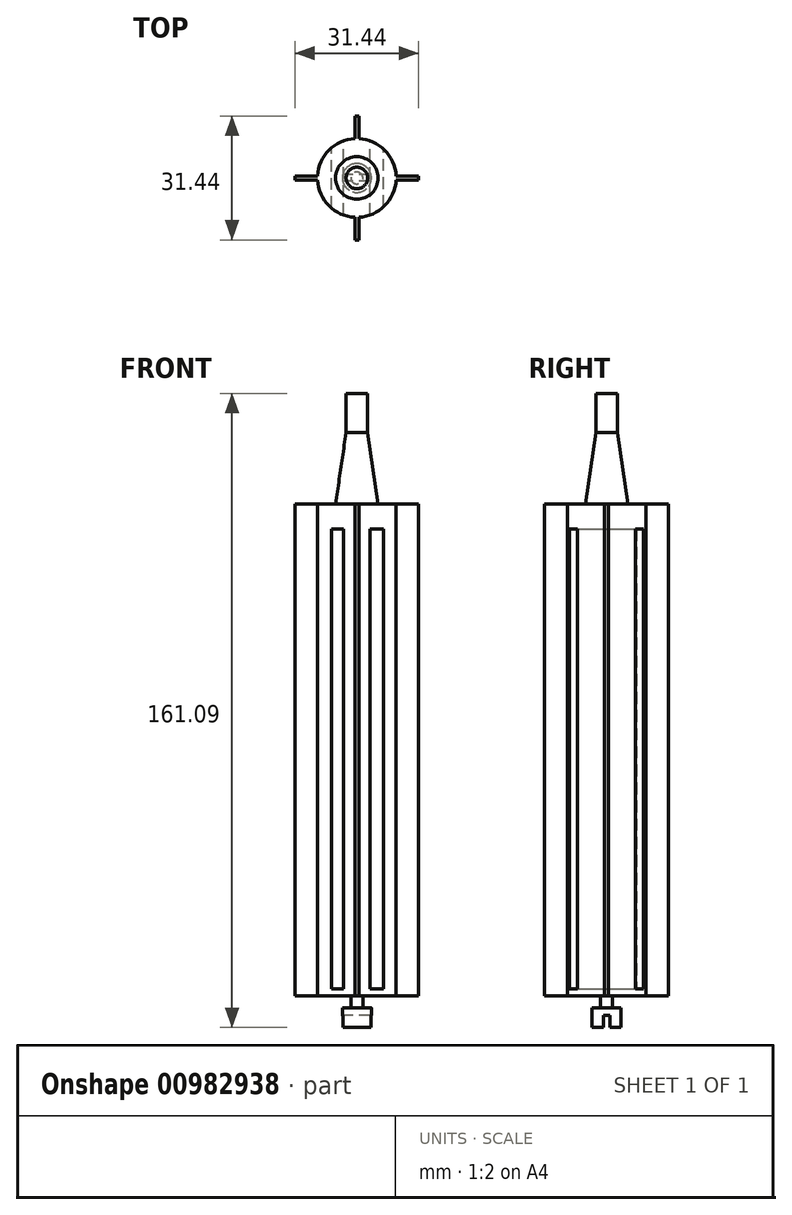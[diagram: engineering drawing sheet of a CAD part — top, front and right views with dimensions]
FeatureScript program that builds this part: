
annotation { "Feature Type Name" : "Feature", "Feature Type Description" : "" }
export const myFeature = defineFeature(function(context is Context, id is Id, definition is map)
    precondition{}
    {
        {
            var Q0;
            Q0=qCreatedBy(makeId("Top.planeOp"),FACE);
            var sketch = newSketch(context, id + "F0", { "sketchPlane" : qUnion([Q0])});
            skCircle(sketch, "E0", {"center": v(0, 0) * mm, "radius": 10 * mm});
            skLineSegment(sketch, "E1.bottom", {"start": v(-0.5, 15.72) * mm, "end": v(0.5, 15.72) * mm});
            skLineSegment(sketch, "E1.top", {"start": v(-0.5, 2) * mm, "end": v(0.5, 2) * mm});
            skLineSegment(sketch, "E1.left", {"start": v(-0.5, 15.72) * mm, "end": v(-0.5, 2) * mm});
            skLineSegment(sketch, "E1.right", {"start": v(0.5, 15.72) * mm, "end": v(0.5, 2) * mm});
            skPoint(sketch, "E2.center", {"position": v(0, -8) * mm});
            skLineSegment(sketch, "E3.1.0", {"start": v(-15.72, -0.5) * mm, "end": v(-2, -0.5) * mm});
            skLineSegment(sketch, "E3.1.1", {"start": v(-15.72, 0.5) * mm, "end": v(-2, 0.5) * mm});
            skLineSegment(sketch, "E3.1.2", {"start": v(-15.72, -0.5) * mm, "end": v(-15.72, 0.5) * mm});
            skLineSegment(sketch, "E3.1.3", {"start": v(-2, -0.5) * mm, "end": v(-2, 0.5) * mm});
            skLineSegment(sketch, "E3.2.0", {"start": v(0.5, -15.72) * mm, "end": v(0.5, -2) * mm});
            skLineSegment(sketch, "E3.2.1", {"start": v(-0.5, -15.72) * mm, "end": v(-0.5, -2) * mm});
            skLineSegment(sketch, "E3.2.2", {"start": v(0.5, -15.72) * mm, "end": v(-0.5, -15.72) * mm});
            skLineSegment(sketch, "E3.2.3", {"start": v(0.5, -2) * mm, "end": v(-0.5, -2) * mm});
            skLineSegment(sketch, "E3.3.0", {"start": v(15.72, 0.5) * mm, "end": v(2, 0.5) * mm});
            skLineSegment(sketch, "E3.3.1", {"start": v(15.72, -0.5) * mm, "end": v(2, -0.5) * mm});
            skLineSegment(sketch, "E3.3.2", {"start": v(15.72, 0.5) * mm, "end": v(15.72, -0.5) * mm});
            skLineSegment(sketch, "E3.3.3", {"start": v(2, 0.5) * mm, "end": v(2, -0.5) * mm});
            skSolve(sketch);
        }
        {
            var Q0;
            {var subQ1=sQuery(id+"F0.wireOp",EDGE,"E1.top");Q0=makeQuery(id+"F0.imprint","IMPRINT",FACE,{"disambiguationData":[TD([[makeQuery(id+"F0.imprint","IMPRINT",EDGE,{"derivedFrom":subQ1}),-1.0]])]});}
            var Q1;
            {var subQ5=sQuery(id+"F0.wireOp",EDGE,"E1.bottom");Q1=makeQuery(id+"F0.imprint","IMPRINT",FACE,{"disambiguationData":[TD([[makeQuery(id+"F0.imprint","IMPRINT",EDGE,{"derivedFrom":subQ5}),-1.0]])]});}
            var Q2;
            {var subQ5=sQuery(id+"F0.wireOp",EDGE,"E1.top");Q2=makeQuery(id+"F0.imprint","IMPRINT",FACE,{"disambiguationData":[TD([[makeQuery(id+"F0.imprint","IMPRINT",EDGE,{"derivedFrom":subQ5}),1.0]])]});}
            var Q3;
            {var subQ5=sQuery(id+"F0.wireOp",EDGE,"E3.1.2");Q3=makeQuery(id+"F0.imprint","IMPRINT",FACE,{"disambiguationData":[TD([[makeQuery(id+"F0.imprint","IMPRINT",EDGE,{"derivedFrom":subQ5}),-1.0]])]});}
            var Q4;
            {var subQ5=sQuery(id+"F0.wireOp",EDGE,"E3.2.2");Q4=makeQuery(id+"F0.imprint","IMPRINT",FACE,{"disambiguationData":[TD([[makeQuery(id+"F0.imprint","IMPRINT",EDGE,{"derivedFrom":subQ5}),-1.0]])]});}
            var Q5;
            {var subQ5=sQuery(id+"F0.wireOp",EDGE,"E3.1.3");Q5=makeQuery(id+"F0.imprint","IMPRINT",FACE,{"disambiguationData":[TD([[makeQuery(id+"F0.imprint","IMPRINT",EDGE,{"derivedFrom":subQ5}),1.0]])]});}
            var Q6;
            {var subQ5=sQuery(id+"F0.wireOp",EDGE,"E3.3.3");Q6=makeQuery(id+"F0.imprint","IMPRINT",FACE,{"disambiguationData":[TD([[makeQuery(id+"F0.imprint","IMPRINT",EDGE,{"derivedFrom":subQ5}),1.0]])]});}
            var Q7;
            {var subQ5=sQuery(id+"F0.wireOp",EDGE,"E3.2.3");Q7=makeQuery(id+"F0.imprint","IMPRINT",FACE,{"disambiguationData":[TD([[makeQuery(id+"F0.imprint","IMPRINT",EDGE,{"derivedFrom":subQ5}),1.0]])]});}
            var Q8;
            {var subQ5=sQuery(id+"F0.wireOp",EDGE,"E3.3.2");Q8=makeQuery(id+"F0.imprint","IMPRINT",FACE,{"disambiguationData":[TD([[makeQuery(id+"F0.imprint","IMPRINT",EDGE,{"derivedFrom":subQ5}),-1.0]])]});}
            extrude(context, id + "F1", {"entities" : qUnion([Q0, Q1, Q2, Q3, Q4, Q5, Q6, Q7, Q8]), "depth" : 125 * mm, "offsetDistance" : 25 * mm});
        }
        {
            var Q0;
            Q0=qCreatedBy(makeId("Front.planeOp"),FACE);
            var sketch = newSketch(context, id + "F2", { "sketchPlane" : qUnion([Q0])});
            skLineSegment(sketch, "E4", {"start": v(2.74, 143.1) * mm, "end": v(5.4, 125) * mm});
            skLineSegment(sketch, "E5", {"start": v(5.4, 125) * mm, "end": v(0, 125) * mm});
            skLineSegment(sketch, "E6", {"start": v(0, 125) * mm, "end": v(0, 143.1) * mm});
            skLineSegment(sketch, "E7", {"start": v(0, 143.1) * mm, "end": v(2.74, 143.1) * mm});
            skSolve(sketch);
        }
        {
            var Q0;
            Q0=makeQuery(id+"F2.imprint","IMPRINT",FACE,{"disambiguationData":[TD([[makeQuery(id+"F2.imprint","IMPRINT",EDGE,{"derivedFrom":sQuery(id+"F2.wireOp",EDGE,"E4")}),-1.0]])]});
            var Q1;
            Q1=sQuery(id+"F2.wireOp",EDGE,"E6");
            revolve(context, id + "F3", {"surfaceOperationType" : NewSurfaceOperationType.NEW, "entities" : qUnion([Q0]), "axis" : qUnion([Q1]), "revolveType" : RevolveType.FULL});
        }
        {
            var Q0;
            Q0=makeQuery(id+"F3.opRevolve","SWEPT_FACE",FACE,{"disambiguationData":[OSD([sQuery(id+"F2.wireOp",EDGE,"E7")])]});
            var sketch = newSketch(context, id + "F4", { "sketchPlane" : qUnion([Q0])});
            skCircle(sketch, "E8", {"center": v(0, 0) * mm, "radius": 2.74 * mm});
            skSolve(sketch);
        }
        {
            var Q0;
            Q0 = qSketchRegion(id + "F4", true);
            extrude(context, id + "F5", {"entities" : qUnion([Q0]), "operationType" : NewBodyOperationType.ADD, "depth" : 10 * mm, "offsetDistance" : 25 * mm});
        }
        {
            var Q0;
            Q0=qCreatedBy(makeId("Front.planeOp"),FACE);
            var sketch = newSketch(context, id + "F6", { "sketchPlane" : qUnion([Q0])});
            skLineSegment(sketch, "E9.bottom", {"start": v(3.33, 118.61) * mm, "end": v(6.76, 118.61) * mm});
            skLineSegment(sketch, "E9.top", {"start": v(3.33, 1.73) * mm, "end": v(6.76, 1.73) * mm});
            skLineSegment(sketch, "E9.left", {"start": v(3.33, 118.61) * mm, "end": v(3.33, 1.73) * mm});
            skLineSegment(sketch, "E9.right", {"start": v(6.76, 118.61) * mm, "end": v(6.76, 1.73) * mm});
            skLineSegment(sketch, "E10.bottom", {"start": v(-3.38, 118.61) * mm, "end": v(-6.5, 118.61) * mm});
            skLineSegment(sketch, "E10.top", {"start": v(-3.38, 1.73) * mm, "end": v(-6.5, 1.73) * mm});
            skLineSegment(sketch, "E10.left", {"start": v(-3.38, 118.61) * mm, "end": v(-3.38, 1.73) * mm});
            skLineSegment(sketch, "E10.right", {"start": v(-6.5, 118.61) * mm, "end": v(-6.5, 1.73) * mm});
            skLineSegment(sketch, "E11", {"start": v(6.76, 97.94) * mm, "end": v(3.33, 97.94) * mm});
            skLineSegment(sketch, "E12", {"start": v(3.33, 97.94) * mm, "end": v(3.33, 96.85) * mm});
            skLineSegment(sketch, "E13", {"start": v(3.33, 96.85) * mm, "end": v(6.76, 96.85) * mm});
            skLineSegment(sketch, "E14", {"start": v(-3.38, 97.94) * mm, "end": v(-6.5, 97.94) * mm});
            skLineSegment(sketch, "E15", {"start": v(-6.5, 97.94) * mm, "end": v(-6.5, 97.15) * mm});
            skLineSegment(sketch, "E16", {"start": v(-3.38, 96.85) * mm, "end": v(-6.5, 96.85) * mm});
            skLineSegment(sketch, "E17.bottom", {"start": v(6.76, 77.78) * mm, "end": v(3.33, 77.78) * mm});
            skLineSegment(sketch, "E17.top", {"start": v(6.76, 76.79) * mm, "end": v(3.33, 76.79) * mm});
            skLineSegment(sketch, "E17.left", {"start": v(6.76, 77.78) * mm, "end": v(6.76, 76.79) * mm});
            skLineSegment(sketch, "E17.right", {"start": v(3.33, 77.78) * mm, "end": v(3.33, 76.79) * mm});
            skLineSegment(sketch, "E18.bottom", {"start": v(-3.38, 77.78) * mm, "end": v(-6.5, 77.78) * mm});
            skLineSegment(sketch, "E18.top", {"start": v(-3.38, 76.79) * mm, "end": v(-6.5, 76.79) * mm});
            skLineSegment(sketch, "E18.left", {"start": v(-3.38, 77.78) * mm, "end": v(-3.38, 76.79) * mm});
            skLineSegment(sketch, "E18.right", {"start": v(-6.5, 77.78) * mm, "end": v(-6.5, 76.79) * mm});
            skSolve(sketch);
        }
        {
            var Q0;
            Q0 = qSketchRegion(id + "F6", true);
            extrude(context, id + "F7", {"entities" : qUnion([Q0]), "operationType" : NewBodyOperationType.REMOVE, "endBound" : BoundingType.SYMMETRIC, "depth" : 25 * mm, "offsetDistance" : 25 * mm});
        }
        {
            var Q0;
            Q0=makeQuery(id+"F1.opExtrude","CAP_FACE",FACE,{"disambiguationData":[OSD([sQuery(id+"F0.wireOp",EDGE,"E0"),sQuery(id+"F0.wireOp",EDGE,"E1.top"),sQuery(id+"F0.wireOp",EDGE,"E1.left"),sQuery(id+"F0.wireOp",EDGE,"E1.right"),sQuery(id+"F0.wireOp",EDGE,"E3.1.0"),sQuery(id+"F0.wireOp",EDGE,"E3.1.1"),sQuery(id+"F0.wireOp",EDGE,"E3.1.3"),sQuery(id+"F0.wireOp",EDGE,"E3.2.0"),sQuery(id+"F0.wireOp",EDGE,"E3.2.1"),sQuery(id+"F0.wireOp",EDGE,"E3.2.3"),sQuery(id+"F0.wireOp",EDGE,"E3.3.0"),sQuery(id+"F0.wireOp",EDGE,"E3.3.1"),sQuery(id+"F0.wireOp",EDGE,"E3.3.3")])],"isStart":true});
            var sketch = newSketch(context, id + "F8", { "sketchPlane" : qUnion([Q0])});
            skCircle(sketch, "E19", {"center": v(0, 0) * mm, "radius": 1.52 * mm});
            skSolve(sketch);
        }
        {
            var Q0;
            Q0=makeQuery(id+"F8.imprint","IMPRINT",FACE,{"disambiguationData":[TD([[makeQuery(id+"F8.imprint","IMPRINT",EDGE,{"derivedFrom":sQuery(id+"F8.wireOp",EDGE,"E19")}),1.0]])]});
            extrude(context, id + "F9", {"entities" : qUnion([Q0]), "operationType" : NewBodyOperationType.ADD, "depth" : 3 * mm, "offsetDistance" : 25 * mm});
        }
        {
            var Q0;
            Q0=makeQuery(id+"F9.opExtrude","CAP_FACE",FACE,{"disambiguationData":[OSD([sQuery(id+"F8.wireOp",EDGE,"E19")])],"isStart":false});
            var sketch = newSketch(context, id + "F10", { "sketchPlane" : qUnion([Q0])});
            skCircle(sketch, "E20", {"center": v(0, 0) * mm, "radius": 3.68 * mm});
            skSolve(sketch);
        }
        {
            var Q0;
            Q0=makeQuery(id+"F10.imprint","IMPRINT",FACE,{"disambiguationData":[TD([[makeQuery(id+"F10.imprint","IMPRINT",EDGE,{"derivedFrom":makeQuery(id+"F9.opExtrude","CAP_EDGE",EDGE,{"disambiguationData":[OSD([sQuery(id+"F8.wireOp",EDGE,"E19")])],"isStart":false})}),1.0]])]});
            var Q1;
            Q1=makeQuery(id+"F10.imprint","IMPRINT",FACE,{"disambiguationData":[TD([[makeQuery(id+"F10.imprint","IMPRINT",EDGE,{"derivedFrom":sQuery(id+"F10.wireOp",EDGE,"E20")}),1.0]])]});
            extrude(context, id + "F11", {"entities" : qUnion([Q0, Q1]), "operationType" : NewBodyOperationType.ADD, "depth" : 5 * mm, "offsetDistance" : 25 * mm});
        }
        {
            var Q0;
            Q0=makeQuery(id+"F11.opExtrude","CAP_FACE",FACE,{"disambiguationData":[OSD([sQuery(id+"F10.wireOp",EDGE,"E20")])],"isStart":false});
            var sketch = newSketch(context, id + "F12", { "sketchPlane" : qUnion([Q0])});
            skLineSegment(sketch, "E21.bottom", {"start": v(4, -0.85) * mm, "end": v(-4, -0.85) * mm});
            skLineSegment(sketch, "E21.top", {"start": v(4, 0.85) * mm, "end": v(-4, 0.85) * mm});
            skLineSegment(sketch, "E21.left", {"start": v(4, -0.85) * mm, "end": v(4, 0.85) * mm});
            skLineSegment(sketch, "E21.right", {"start": v(-4, -0.85) * mm, "end": v(-4, 0.85) * mm});
            skPoint(sketch, "E21.middle", {"position": v(0, 0) * mm});
            skSolve(sketch);
        }
        {
            var Q0;
            Q0 = qSketchRegion(id + "F12", true);
            extrude(context, id + "F13", {"entities" : qUnion([Q0]), "operationType" : NewBodyOperationType.REMOVE, "oppositeDirection" : true, "depth" : 3 * mm, "offsetDistance" : 25 * mm});
        }
        {
            var Q0;
            Q0=makeQuery(id+"F5.opExtrude","CAP_FACE",FACE,{"disambiguationData":[OSD([sQuery(id+"F4.wireOp",EDGE,"E8")])],"isStart":false});
            var sketch = newSketch(context, id + "F14", { "sketchPlane" : qUnion([Q0])});
            skCircle(sketch, "E22", {"center": v(0, 0) * mm, "radius": 1.37 * mm});
            skSolve(sketch);
        }
        {
            var Q0;
            Q0 = qSketchRegion(id + "F14", true);
            extrude(context, id + "F15", {"entities" : qUnion([Q0]), "operationType" : NewBodyOperationType.ADD, "oppositeDirection" : true, "depth" : 25 * mm, "offsetDistance" : 25 * mm});
        }
    });
